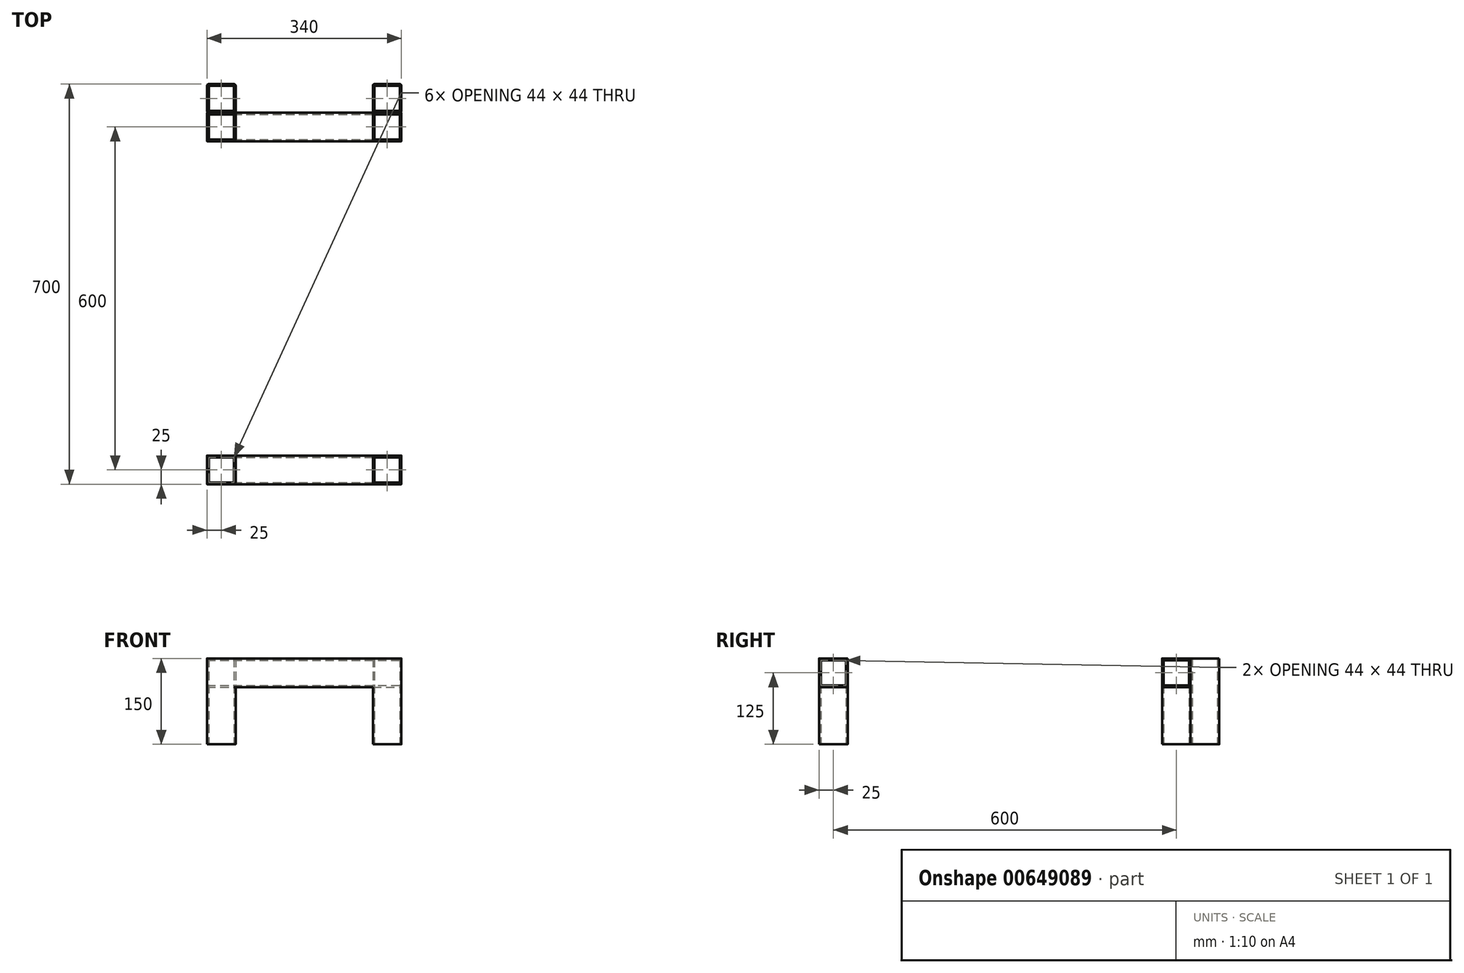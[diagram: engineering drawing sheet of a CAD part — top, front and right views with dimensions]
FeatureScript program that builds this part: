
annotation { "Feature Type Name" : "Feature", "Feature Type Description" : "" }
export const myFeature = defineFeature(function(context is Context, id is Id, definition is map)
    precondition{}
    {
        {
            var Q0;
            Q0=qCreatedBy(makeId("Top.planeOp"),FACE);
            cPlane(context, id + "F0", {"entities" : qUnion([Q0]), "cplaneType" : CPlaneType.OFFSET, "offset" : 50 * mm, "width" : 150 * mm, "height" : 150 * mm});
        }
        {
            var Q0;
            Q0=qCreatedBy(id+"F0.planeOp",FACE);
            var sketch = newSketch(context, id + "F1", { "sketchPlane" : qUnion([Q0])});
            skLineSegment(sketch, "E0.bottom", {"start": v(123, -300) * mm, "end": v(167, -300) * mm});
            skLineSegment(sketch, "E0.top", {"start": v(123, -250) * mm, "end": v(167, -250) * mm});
            skLineSegment(sketch, "E0.left", {"start": v(120, -297) * mm, "end": v(120, -253) * mm});
            skLineSegment(sketch, "E0.right", {"start": v(170, -297) * mm, "end": v(170, -253) * mm});
            skLineSegment(sketch, "E1.bottom", {"start": v(123, 300) * mm, "end": v(167, 300) * mm});
            skLineSegment(sketch, "E1.top", {"start": v(123, 350) * mm, "end": v(167, 350) * mm});
            skLineSegment(sketch, "E1.left", {"start": v(120, 303) * mm, "end": v(120, 347) * mm});
            skLineSegment(sketch, "E1.right", {"start": v(170, 303) * mm, "end": v(170, 347) * mm});
            skLineSegment(sketch, "E2.bottom", {"start": v(-167, -300) * mm, "end": v(-123, -300) * mm});
            skLineSegment(sketch, "E2.top", {"start": v(-167, -250) * mm, "end": v(-123, -250) * mm});
            skLineSegment(sketch, "E2.left", {"start": v(-170, -297) * mm, "end": v(-170, -253) * mm});
            skLineSegment(sketch, "E2.right", {"start": v(-120, -297) * mm, "end": v(-120, -253) * mm});
            skLineSegment(sketch, "E3.bottom", {"start": v(-167, 300) * mm, "end": v(-123, 300) * mm});
            skLineSegment(sketch, "E3.top", {"start": v(-167, 350) * mm, "end": v(-123, 350) * mm});
            skLineSegment(sketch, "E3.left", {"start": v(-170, 303) * mm, "end": v(-170, 347) * mm});
            skLineSegment(sketch, "E3.right", {"start": v(-120, 303) * mm, "end": v(-120, 347) * mm});
            skLineSegment(sketch, "E4.0", {"start": v(-123, -295.5) * mm, "end": v(-123, -254.5) * mm});
            skLineSegment(sketch, "E4.1", {"start": v(-165.5, -297) * mm, "end": v(-124.5, -297) * mm});
            skLineSegment(sketch, "E4.2", {"start": v(-167, -295.5) * mm, "end": v(-167, -254.5) * mm});
            skLineSegment(sketch, "E4.3", {"start": v(-165.5, -253) * mm, "end": v(-124.5, -253) * mm});
            skLineSegment(sketch, "E5.0", {"start": v(-167, 304.5) * mm, "end": v(-167, 345.5) * mm});
            skLineSegment(sketch, "E5.1", {"start": v(-165.5, 303) * mm, "end": v(-124.5, 303) * mm});
            skLineSegment(sketch, "E5.2", {"start": v(-123, 304.5) * mm, "end": v(-123, 345.5) * mm});
            skLineSegment(sketch, "E5.3", {"start": v(-165.5, 347) * mm, "end": v(-124.5, 347) * mm});
            skLineSegment(sketch, "E6.0", {"start": v(167, -295.5) * mm, "end": v(167, -254.5) * mm});
            skLineSegment(sketch, "E6.1", {"start": v(124.5, -297) * mm, "end": v(165.5, -297) * mm});
            skLineSegment(sketch, "E6.2", {"start": v(123, -295.5) * mm, "end": v(123, -254.5) * mm});
            skLineSegment(sketch, "E6.3", {"start": v(124.5, -253) * mm, "end": v(165.5, -253) * mm});
            skLineSegment(sketch, "E7.0", {"start": v(167, 304.5) * mm, "end": v(167, 345.5) * mm});
            skLineSegment(sketch, "E7.1", {"start": v(124.5, 303) * mm, "end": v(165.5, 303) * mm});
            skLineSegment(sketch, "E7.2", {"start": v(123, 304.5) * mm, "end": v(123, 345.5) * mm});
            skLineSegment(sketch, "E7.3", {"start": v(124.5, 347) * mm, "end": v(165.5, 347) * mm});
            skPoint(sketch, "E8.visualSharp", {"position": v(-170, -300) * mm});
            skArc(sketch, "E8.filletArc", {"start": v(-170, -297) * mm, "mid": v(-169.12, -299.12) * mm, "end": v(-167, -300) * mm});
            skPoint(sketch, "E9.visualSharp", {"position": v(-170, -250) * mm});
            skArc(sketch, "E9.filletArc", {"start": v(-167, -250) * mm, "mid": v(-169.12, -250.88) * mm, "end": v(-170, -253) * mm});
            skPoint(sketch, "E10.visualSharp", {"position": v(-120, -250) * mm});
            skArc(sketch, "E10.filletArc", {"start": v(-120, -253) * mm, "mid": v(-120.88, -250.88) * mm, "end": v(-123, -250) * mm});
            skPoint(sketch, "E11.visualSharp", {"position": v(-120, -300) * mm});
            skArc(sketch, "E11.filletArc", {"start": v(-123, -300) * mm, "mid": v(-120.88, -299.12) * mm, "end": v(-120, -297) * mm});
            skPoint(sketch, "E12.visualSharp", {"position": v(120, -300) * mm});
            skArc(sketch, "E12.filletArc", {"start": v(120, -297) * mm, "mid": v(120.88, -299.12) * mm, "end": v(123, -300) * mm});
            skPoint(sketch, "E13.visualSharp", {"position": v(120, -250) * mm});
            skArc(sketch, "E13.filletArc", {"start": v(123, -250) * mm, "mid": v(120.88, -250.88) * mm, "end": v(120, -253) * mm});
            skPoint(sketch, "E14.visualSharp", {"position": v(170, -250) * mm});
            skArc(sketch, "E14.filletArc", {"start": v(170, -253) * mm, "mid": v(169.12, -250.88) * mm, "end": v(167, -250) * mm});
            skPoint(sketch, "E15.visualSharp", {"position": v(170, -300) * mm});
            skArc(sketch, "E15.filletArc", {"start": v(167, -300) * mm, "mid": v(169.12, -299.12) * mm, "end": v(170, -297) * mm});
            skPoint(sketch, "E16.visualSharp", {"position": v(120, 300) * mm});
            skArc(sketch, "E16.filletArc", {"start": v(120, 303) * mm, "mid": v(120.88, 300.88) * mm, "end": v(123, 300) * mm});
            skPoint(sketch, "E17.visualSharp", {"position": v(120, 350) * mm});
            skArc(sketch, "E17.filletArc", {"start": v(123, 350) * mm, "mid": v(120.88, 349.12) * mm, "end": v(120, 347) * mm});
            skPoint(sketch, "E18.visualSharp", {"position": v(170, 350) * mm});
            skArc(sketch, "E18.filletArc", {"start": v(170, 347) * mm, "mid": v(169.12, 349.12) * mm, "end": v(167, 350) * mm});
            skPoint(sketch, "E19.visualSharp", {"position": v(170, 300) * mm});
            skArc(sketch, "E19.filletArc", {"start": v(167, 300) * mm, "mid": v(169.12, 300.88) * mm, "end": v(170, 303) * mm});
            skPoint(sketch, "E20.visualSharp", {"position": v(-170, 300) * mm});
            skArc(sketch, "E20.filletArc", {"start": v(-170, 303) * mm, "mid": v(-169.12, 300.88) * mm, "end": v(-167, 300) * mm});
            skPoint(sketch, "E21.visualSharp", {"position": v(-170, 350) * mm});
            skArc(sketch, "E21.filletArc", {"start": v(-167, 350) * mm, "mid": v(-169.12, 349.12) * mm, "end": v(-170, 347) * mm});
            skPoint(sketch, "E22.visualSharp", {"position": v(-120, 350) * mm});
            skArc(sketch, "E22.filletArc", {"start": v(-120, 347) * mm, "mid": v(-120.88, 349.12) * mm, "end": v(-123, 350) * mm});
            skPoint(sketch, "E23.visualSharp", {"position": v(-120, 300) * mm});
            skArc(sketch, "E23.filletArc", {"start": v(-123, 300) * mm, "mid": v(-120.88, 300.88) * mm, "end": v(-120, 303) * mm});
            skArc(sketch, "E24.filletArc", {"start": v(-167, 304.5) * mm, "mid": v(-166.56, 303.44) * mm, "end": v(-165.5, 303) * mm});
            skArc(sketch, "E25.filletArc", {"start": v(-165.5, 347) * mm, "mid": v(-166.56, 346.56) * mm, "end": v(-167, 345.5) * mm});
            skArc(sketch, "E26.filletArc", {"start": v(-123, 345.5) * mm, "mid": v(-123.44, 346.56) * mm, "end": v(-124.5, 347) * mm});
            skArc(sketch, "E27.filletArc", {"start": v(-124.5, 303) * mm, "mid": v(-123.44, 303.44) * mm, "end": v(-123, 304.5) * mm});
            skArc(sketch, "E28.filletArc", {"start": v(123, 304.5) * mm, "mid": v(123.44, 303.44) * mm, "end": v(124.5, 303) * mm});
            skArc(sketch, "E29.filletArc", {"start": v(124.5, 347) * mm, "mid": v(123.44, 346.56) * mm, "end": v(123, 345.5) * mm});
            skArc(sketch, "E30.filletArc", {"start": v(167, 345.5) * mm, "mid": v(166.56, 346.56) * mm, "end": v(165.5, 347) * mm});
            skArc(sketch, "E31.filletArc", {"start": v(165.5, 303) * mm, "mid": v(166.56, 303.44) * mm, "end": v(167, 304.5) * mm});
            skArc(sketch, "E32.filletArc", {"start": v(123, -295.5) * mm, "mid": v(123.44, -296.56) * mm, "end": v(124.5, -297) * mm});
            skArc(sketch, "E33.filletArc", {"start": v(124.5, -253) * mm, "mid": v(123.44, -253.44) * mm, "end": v(123, -254.5) * mm});
            skArc(sketch, "E34.filletArc", {"start": v(167, -254.5) * mm, "mid": v(166.56, -253.44) * mm, "end": v(165.5, -253) * mm});
            skArc(sketch, "E35.filletArc", {"start": v(165.5, -297) * mm, "mid": v(166.56, -296.56) * mm, "end": v(167, -295.5) * mm});
            skArc(sketch, "E36.filletArc", {"start": v(-167, -295.5) * mm, "mid": v(-166.56, -296.56) * mm, "end": v(-165.5, -297) * mm});
            skArc(sketch, "E37.filletArc", {"start": v(-165.5, -253) * mm, "mid": v(-166.56, -253.44) * mm, "end": v(-167, -254.5) * mm});
            skArc(sketch, "E38.filletArc", {"start": v(-123, -254.5) * mm, "mid": v(-123.44, -253.44) * mm, "end": v(-124.5, -253) * mm});
            skArc(sketch, "E39.filletArc", {"start": v(-124.5, -297) * mm, "mid": v(-123.44, -296.56) * mm, "end": v(-123, -295.5) * mm});
            skSolve(sketch);
        }
        {
            var Q0;
            Q0=makeQuery(id+"F1.imprint","IMPRINT",FACE,{"disambiguationData":[TD([[makeQuery(id+"F1.imprint","IMPRINT",EDGE,{"derivedFrom":sQuery(id+"F1.wireOp",EDGE,"E2.bottom")}),1.0]])]});
            var Q1;
            Q1=makeQuery(id+"F1.imprint","IMPRINT",FACE,{"disambiguationData":[TD([[makeQuery(id+"F1.imprint","IMPRINT",EDGE,{"derivedFrom":sQuery(id+"F1.wireOp",EDGE,"E0.bottom")}),1.0]])]});
            var Q2;
            Q2=makeQuery(id+"F1.imprint","IMPRINT",FACE,{"disambiguationData":[TD([[makeQuery(id+"F1.imprint","IMPRINT",EDGE,{"derivedFrom":sQuery(id+"F1.wireOp",EDGE,"E3.bottom")}),1.0]])]});
            var Q3;
            Q3=makeQuery(id+"F1.imprint","IMPRINT",FACE,{"disambiguationData":[TD([[makeQuery(id+"F1.imprint","IMPRINT",EDGE,{"derivedFrom":sQuery(id+"F1.wireOp",EDGE,"E1.bottom")}),1.0]])]});
            extrude(context, id + "F2", {"entities" : qUnion([Q0, Q1, Q2, Q3]), "flatOperationType" : FlatOperationType.REMOVE, "depth" : 150 * mm, "offsetDistance" : 25 * mm, "domain" : OperationDomain.MODEL});
        }
        {
            var Q0;
            Q0=qCreatedBy(makeId("Right.planeOp"),FACE);
            cPlane(context, id + "F3", {"entities" : qUnion([Q0]), "cplaneType" : CPlaneType.OFFSET, "offset" : 170 * mm, "width" : 150 * mm, "height" : 150 * mm});
        }
        {
            var Q0;
            Q0=qCreatedBy(id+"F3.planeOp",FACE);
            var sketch = newSketch(context, id + "F4", { "sketchPlane" : qUnion([Q0])});
            skLineSegment(sketch, "E40.bottom", {"start": v(-297, 200) * mm, "end": v(-253, 200) * mm});
            skLineSegment(sketch, "E40.top", {"start": v(-297, 150) * mm, "end": v(-253, 150) * mm});
            skLineSegment(sketch, "E40.left", {"start": v(-300, 197) * mm, "end": v(-300, 153) * mm});
            skLineSegment(sketch, "E40.right", {"start": v(-250, 197) * mm, "end": v(-250, 153) * mm});
            skLineSegment(sketch, "E41.bottom", {"start": v(303, 200) * mm, "end": v(347, 200) * mm});
            skLineSegment(sketch, "E41.top", {"start": v(303, 150) * mm, "end": v(347, 150) * mm});
            skLineSegment(sketch, "E41.left", {"start": v(300, 197) * mm, "end": v(300, 153) * mm});
            skLineSegment(sketch, "E41.right", {"start": v(350, 197) * mm, "end": v(350, 153) * mm});
            skLineSegment(sketch, "E42.0", {"start": v(-297, 195.5) * mm, "end": v(-297, 154.5) * mm});
            skLineSegment(sketch, "E42.1", {"start": v(-295.5, 197) * mm, "end": v(-254.5, 197) * mm});
            skLineSegment(sketch, "E42.2", {"start": v(-253, 195.5) * mm, "end": v(-253, 154.5) * mm});
            skLineSegment(sketch, "E42.3", {"start": v(-295.5, 153) * mm, "end": v(-254.5, 153) * mm});
            skLineSegment(sketch, "E43.0", {"start": v(303, 195.5) * mm, "end": v(303, 154.5) * mm});
            skLineSegment(sketch, "E43.1", {"start": v(304.5, 197) * mm, "end": v(345.5, 197) * mm});
            skLineSegment(sketch, "E43.2", {"start": v(347, 195.5) * mm, "end": v(347, 154.5) * mm});
            skLineSegment(sketch, "E43.3", {"start": v(304.5, 153) * mm, "end": v(345.5, 153) * mm});
            skPoint(sketch, "E44.visualSharp", {"position": v(-300, 200) * mm});
            skArc(sketch, "E44.filletArc", {"start": v(-297, 200) * mm, "mid": v(-299.12, 199.12) * mm, "end": v(-300, 197) * mm});
            skPoint(sketch, "E45.visualSharp", {"position": v(-250, 200) * mm});
            skArc(sketch, "E45.filletArc", {"start": v(-250, 197) * mm, "mid": v(-250.88, 199.12) * mm, "end": v(-253, 200) * mm});
            skPoint(sketch, "E46.visualSharp", {"position": v(-250, 150) * mm});
            skArc(sketch, "E46.filletArc", {"start": v(-253, 150) * mm, "mid": v(-250.88, 150.88) * mm, "end": v(-250, 153) * mm});
            skPoint(sketch, "E47.visualSharp", {"position": v(-300, 150) * mm});
            skArc(sketch, "E47.filletArc", {"start": v(-300, 153) * mm, "mid": v(-299.12, 150.88) * mm, "end": v(-297, 150) * mm});
            skPoint(sketch, "E48.visualSharp", {"position": v(300, 200) * mm});
            skArc(sketch, "E48.filletArc", {"start": v(303, 200) * mm, "mid": v(300.88, 199.12) * mm, "end": v(300, 197) * mm});
            skPoint(sketch, "E49.visualSharp", {"position": v(350, 200) * mm});
            skArc(sketch, "E49.filletArc", {"start": v(350, 197) * mm, "mid": v(349.12, 199.12) * mm, "end": v(347, 200) * mm});
            skPoint(sketch, "E50.visualSharp", {"position": v(350, 150) * mm});
            skArc(sketch, "E50.filletArc", {"start": v(347, 150) * mm, "mid": v(349.12, 150.88) * mm, "end": v(350, 153) * mm});
            skPoint(sketch, "E51.visualSharp", {"position": v(300, 150) * mm});
            skArc(sketch, "E51.filletArc", {"start": v(300, 153) * mm, "mid": v(300.88, 150.88) * mm, "end": v(303, 150) * mm});
            skArc(sketch, "E52.filletArc", {"start": v(-295.5, 197) * mm, "mid": v(-296.56, 196.56) * mm, "end": v(-297, 195.5) * mm});
            skArc(sketch, "E53.filletArc", {"start": v(-253, 195.5) * mm, "mid": v(-253.44, 196.56) * mm, "end": v(-254.5, 197) * mm});
            skArc(sketch, "E54.filletArc", {"start": v(-254.5, 153) * mm, "mid": v(-253.44, 153.44) * mm, "end": v(-253, 154.5) * mm});
            skArc(sketch, "E55.filletArc", {"start": v(-297, 154.5) * mm, "mid": v(-296.56, 153.44) * mm, "end": v(-295.5, 153) * mm});
            skArc(sketch, "E56.filletArc", {"start": v(304.5, 197) * mm, "mid": v(303.44, 196.56) * mm, "end": v(303, 195.5) * mm});
            skArc(sketch, "E57.filletArc", {"start": v(347, 195.5) * mm, "mid": v(346.56, 196.56) * mm, "end": v(345.5, 197) * mm});
            skArc(sketch, "E58.filletArc", {"start": v(345.5, 153) * mm, "mid": v(346.56, 153.44) * mm, "end": v(347, 154.5) * mm});
            skArc(sketch, "E59.filletArc", {"start": v(303, 154.5) * mm, "mid": v(303.44, 153.44) * mm, "end": v(304.5, 153) * mm});
            skSolve(sketch);
        }
        {
            var Q0;
            Q0=makeQuery(id+"F4.imprint","IMPRINT",FACE,{"disambiguationData":[TD([[makeQuery(id+"F4.imprint","IMPRINT",EDGE,{"derivedFrom":sQuery(id+"F4.wireOp",EDGE,"E40.bottom")}),-1.0]])]});
            var Q1;
            Q1=makeQuery(id+"F4.imprint","IMPRINT",FACE,{"disambiguationData":[TD([[makeQuery(id+"F4.imprint","IMPRINT",EDGE,{"derivedFrom":sQuery(id+"F4.wireOp",EDGE,"E41.bottom")}),-1.0]])]});
            extrude(context, id + "F5", {"entities" : qUnion([Q0, Q1]), "oppositeDirection" : true, "depth" : 340 * mm, "offsetDistance" : 25 * mm});
        }
        {
            var Q0;
            Q0=qCreatedBy(id+"F0.planeOp",FACE);
            var sketch = newSketch(context, id + "F6", { "sketchPlane" : qUnion([Q0])});
            skLineSegment(sketch, "E60.bottom", {"start": v(-167, 400) * mm, "end": v(-123, 400) * mm});
            skLineSegment(sketch, "E60.top", {"start": v(-167, 350) * mm, "end": v(-123, 350) * mm});
            skLineSegment(sketch, "E60.left", {"start": v(-170, 397) * mm, "end": v(-170, 353) * mm});
            skLineSegment(sketch, "E60.right", {"start": v(-120, 397) * mm, "end": v(-120, 353) * mm});
            skLineSegment(sketch, "E61.bottom", {"start": v(123, 350) * mm, "end": v(167, 350) * mm});
            skLineSegment(sketch, "E61.top", {"start": v(123, 400) * mm, "end": v(167, 400) * mm});
            skLineSegment(sketch, "E61.left", {"start": v(120, 353) * mm, "end": v(120, 397) * mm});
            skLineSegment(sketch, "E61.right", {"start": v(170, 353) * mm, "end": v(170, 397) * mm});
            skLineSegment(sketch, "E62.0", {"start": v(-165.5, 353) * mm, "end": v(-124.5, 353) * mm});
            skLineSegment(sketch, "E62.1", {"start": v(-167, 395.5) * mm, "end": v(-167, 354.5) * mm});
            skLineSegment(sketch, "E62.2", {"start": v(-165.5, 397) * mm, "end": v(-124.5, 397) * mm});
            skLineSegment(sketch, "E62.3", {"start": v(-123, 395.5) * mm, "end": v(-123, 354.5) * mm});
            skLineSegment(sketch, "E63.0", {"start": v(124.5, 353) * mm, "end": v(165.5, 353) * mm});
            skLineSegment(sketch, "E63.1", {"start": v(123, 354.5) * mm, "end": v(123, 395.5) * mm});
            skLineSegment(sketch, "E63.2", {"start": v(124.5, 397) * mm, "end": v(165.5, 397) * mm});
            skLineSegment(sketch, "E63.3", {"start": v(167, 354.5) * mm, "end": v(167, 395.5) * mm});
            skPoint(sketch, "E64.visualSharp", {"position": v(120, 400) * mm});
            skArc(sketch, "E64.filletArc", {"start": v(123, 400) * mm, "mid": v(120.88, 399.12) * mm, "end": v(120, 397) * mm});
            skPoint(sketch, "E65.visualSharp", {"position": v(170, 400) * mm});
            skArc(sketch, "E65.filletArc", {"start": v(170, 397) * mm, "mid": v(169.12, 399.12) * mm, "end": v(167, 400) * mm});
            skPoint(sketch, "E66.visualSharp", {"position": v(170, 350) * mm});
            skArc(sketch, "E66.filletArc", {"start": v(167, 350) * mm, "mid": v(169.12, 350.88) * mm, "end": v(170, 353) * mm});
            skPoint(sketch, "E67.visualSharp", {"position": v(120, 350) * mm});
            skArc(sketch, "E67.filletArc", {"start": v(120, 353) * mm, "mid": v(120.88, 350.88) * mm, "end": v(123, 350) * mm});
            skPoint(sketch, "E68.visualSharp", {"position": v(-170, 400) * mm});
            skArc(sketch, "E68.filletArc", {"start": v(-167, 400) * mm, "mid": v(-169.12, 399.12) * mm, "end": v(-170, 397) * mm});
            skPoint(sketch, "E69.visualSharp", {"position": v(-120, 400) * mm});
            skArc(sketch, "E69.filletArc", {"start": v(-120, 397) * mm, "mid": v(-120.88, 399.12) * mm, "end": v(-123, 400) * mm});
            skPoint(sketch, "E70.visualSharp", {"position": v(-120, 350) * mm});
            skArc(sketch, "E70.filletArc", {"start": v(-123, 350) * mm, "mid": v(-120.88, 350.88) * mm, "end": v(-120, 353) * mm});
            skPoint(sketch, "E71.visualSharp", {"position": v(-170, 350) * mm});
            skArc(sketch, "E71.filletArc", {"start": v(-170, 353) * mm, "mid": v(-169.12, 350.88) * mm, "end": v(-167, 350) * mm});
            skArc(sketch, "E72.filletArc", {"start": v(-165.5, 397) * mm, "mid": v(-166.56, 396.56) * mm, "end": v(-167, 395.5) * mm});
            skArc(sketch, "E73.filletArc", {"start": v(-123, 395.5) * mm, "mid": v(-123.44, 396.56) * mm, "end": v(-124.5, 397) * mm});
            skArc(sketch, "E74.filletArc", {"start": v(-124.5, 353) * mm, "mid": v(-123.44, 353.44) * mm, "end": v(-123, 354.5) * mm});
            skArc(sketch, "E75.filletArc", {"start": v(-167, 354.5) * mm, "mid": v(-166.56, 353.44) * mm, "end": v(-165.5, 353) * mm});
            skArc(sketch, "E76.filletArc", {"start": v(124.5, 397) * mm, "mid": v(123.44, 396.56) * mm, "end": v(123, 395.5) * mm});
            skArc(sketch, "E77.filletArc", {"start": v(167, 395.5) * mm, "mid": v(166.56, 396.56) * mm, "end": v(165.5, 397) * mm});
            skArc(sketch, "E78.filletArc", {"start": v(165.5, 353) * mm, "mid": v(166.56, 353.44) * mm, "end": v(167, 354.5) * mm});
            skArc(sketch, "E79.filletArc", {"start": v(123, 354.5) * mm, "mid": v(123.44, 353.44) * mm, "end": v(124.5, 353) * mm});
            skSolve(sketch);
        }
        {
            var Q0;
            Q0=makeQuery(id+"F6.imprint","IMPRINT",FACE,{"disambiguationData":[TD([[makeQuery(id+"F6.imprint","IMPRINT",EDGE,{"derivedFrom":sQuery(id+"F6.wireOp",EDGE,"E60.bottom")}),-1.0]])]});
            var Q1;
            Q1=makeQuery(id+"F6.imprint","IMPRINT",FACE,{"disambiguationData":[TD([[makeQuery(id+"F6.imprint","IMPRINT",EDGE,{"derivedFrom":sQuery(id+"F6.wireOp",EDGE,"E61.bottom")}),1.0]])]});
            extrude(context, id + "F7", {"entities" : qUnion([Q0, Q1]), "depth" : 150 * mm, "offsetDistance" : 25 * mm});
        }
    });
